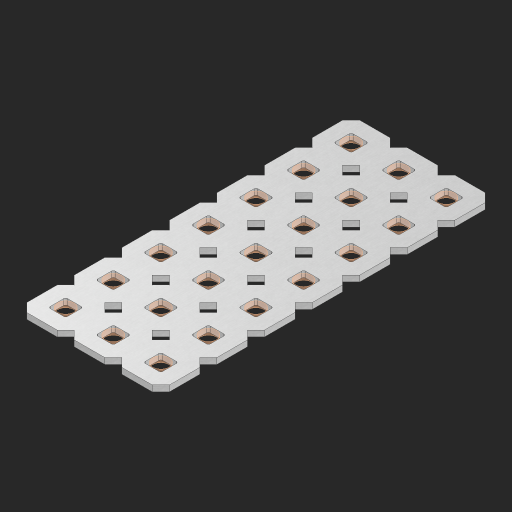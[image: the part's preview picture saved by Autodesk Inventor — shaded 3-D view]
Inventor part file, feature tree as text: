
AUTODESK INVENTOR PART (.ipt)
format: ipt  version: 2023 (Build 270158000, 158)  size: 536,064 bytes
history: native  units: in
note: dims shown in document units (in); Inventor stores cm internally (conversion verified against a paired STEP export)
features: other x22, extrude x20, sketch x2, pattern_linear x1
ambient origin geometry x8: Origin, YZ Plane, XZ Plane, XY Plane, X Axis, Y Axis, Z Axis, Center Point
bodies: Solid1 (feature_tree), Body (feature_tree)
feature tree (45):
  pattern_linear  "Rectangular Pattern1"  Spacing1=0.09in  [1 undecoded]
  sketch  "Sketch1"  dims[d1=0.5in]
  sketch  "Sketch2"  dims[d2=0.182in d3=0.09in d4=0.09in d5=0.09in d6=0.09in d7=0.09in d8=0.09in d9=0.09in d10=0.09in d11=0.02in d13=0.0in d14=0.172in d15=0.0625in d16=0.0in d19=0.5in d22=0.5in]
  other  "Srf1"
  other  "Srf126"
  other  "Srf127"
  other  "Srf128"
  other  "Srf129"
  other  "Srf130"
  other  "Srf131"
  other  "Srf268"
  other  "Srf269"
  other  "Srf270"
  other  "Srf271"
  other  "Srf272"
  other  "Srf273"
  other  "Srf274"
  other  "Srf293"
  other  "Srf294"
  other  "Srf295"
  other  "Srf296"
  other  "Srf297"
  other  "Srf298"
  other  "Srf299"
  other  "Circle"
  extrude  "ExtrusionSrf126"  Depth=0.09in
  extrude  "ExtrusionSrf127"  Depth=0.09in
  extrude  "ExtrusionSrf128"  Depth=0.09in
  extrude  "ExtrusionSrf129"  Depth=0.09in
  extrude  "ExtrusionSrf130"  Depth=0.09in
  extrude  "ExtrusionSrf131"  Depth=0.09in
  extrude  "ExtrusionSrf268"  Depth=0.09in
  extrude  "ExtrusionSrf269"  Depth=0.02in
  extrude  "ExtrusionSrf270"  TaperAngle=0.0deg  [1 undecoded]
  extrude  "ExtrusionSrf271"  Depth=0.5in
  extrude  "ExtrusionSrf272"  Depth=0.0625in TaperAngle=0.0deg
  extrude  "ExtrusionSrf273"  Depth=0.5in
  extrude  "ExtrusionSrf274"  Depth=0.5in
  extrude  "ExtrusionSrf293"  [1 undecoded]
  extrude  "ExtrusionSrf294"  [1 undecoded]
  extrude  "ExtrusionSrf295"  [1 undecoded]
  extrude  "ExtrusionSrf296"  [1 undecoded]
  extrude  "ExtrusionSrf297"  [1 undecoded]
  extrude  "ExtrusionSrf298"  [1 undecoded]
  extrude  "ExtrusionSrf299"  [1 undecoded]
note: 9 required parameter values undecoded (feature->parameter linkage not recoverable at this tier; creation-order binding heuristic only, values carry confidence <= 0.55)
